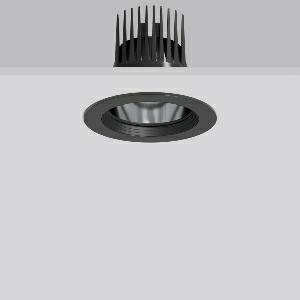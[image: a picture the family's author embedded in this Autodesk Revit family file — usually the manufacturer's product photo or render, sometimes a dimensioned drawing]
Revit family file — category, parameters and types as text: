
# Revit family: heledon_maxi_e_901771_003_3608
name_source: partatom
category: Lighting Fixtures
units: mm (PartAtom-declared; Revit-internal decimal feet)

## family parameters
Cut with Voids When Loaded = No
Host = Face
Light Source = No
Part Type = Normal
Room Calculation Point = No
Round Connector Dimension = Use Diameter
Shared = No

## types (1)
- HELEDON maxi E (1 x LED Modul 932 fresh meat, 2150 lm, 3200)
    Apparent Load = 33 VA
    Approval mark = CE
    CIE Flux Codes = 100 100 100 100 100
    Color Rendering = 90
    Color Temperature = 3200
    Default Elevation = 1800 mm
    Description = Series: HELEDON maxi
Round recessed downlight. Housing: die-cast aluminium, powder-coated. Black plastic ring and recessed LED to prevent glare from the side. Optical assembly with reflector made of MIRO-Silver with 98% total light reflection for outstanding efficiency - can be changed without tools. Special LED for illumination of meat included. Suitable for Recessed ceiling mounting. Installation without tools thanks to spring fastening system. Including separate LED converter with connecting cable 600 mm.High quality converter without flickering and stroboscopic effect. Through-wiring box (5 pole) available as accessory. The following accessories can be mounted without use of tools: interchangeable lenses, decorative glasses, honeycomb louvre, clear and frosted diffusers, white interchangeable plastic ring. 
Colour: deep black, matt (RAL 9005)
Diameter: 162 mm
Height: 3 mm
Cut-out diameter: 152 mm
Recess height: 200 mm
Luminaire: recess height: 135 mm
Lamp: LED
Socket: without socket
Colour temperature: fresh meat
System power: 33 W
Rated luminous flux: 2150 lm
Luminous efficiency: 65 lm/W
Control gear: Regulated power supply
Protection class: II
Type of protection: IP 20
    Height = 0 mm  [stored 0 ft]
    Lamp = 1 x LED Modul 932 fresh meat
    Lamp Light Flux = 2150 lm
    Lamp count = 1
    Length = 162 mm
    Lifetime = 50000 h
    Luminous efficacy = 65 lm/W
    Manufacturer = RZB
    ModVariant = No
    Model = 901771.003
    Mounting Place = Ceiling
    Mounting Type = Recessed
    Number of Poles = 1
    OnlyDefault = Yes
    Power Factor = 1
    Product Name = HELEDON maxi E
    Product group = Recessed downlights
    ProductGroupID = 402
    Protection Class = Protection class II
    Protection Degree = IP 20
    RLX_Detail_Level = 1
    RLX_Emergency_Light_Flux = 0 lm
    RLX_Emergency_Type = 0
    RLX_Emergency_Type_DB = No
    RlxData = <blob elided: 122009 chars, md5=d6250a78>
    Socket = socket
    Standby Power = 0 W
    System Light Flux = 2150 lm
    System Power = 33 W
    Type Comments = Product without accessories
    Type Image = 901662.003.jpg
    URL = http://relux.com
    VarID = ---
    Voltage = 230 V
    Voltage Range = 220-240 V
    Weight = 0.00 kg
    Width = 0 mm  [stored 0 ft]

note: [stored X ft] marks values corroborated as IEEE doubles in the binary element streams (Revit-internal decimal feet)

## geometry (parser evidence)
native form markers: Blend x4, Sweep x12
no freeform markers — native parametric forms only
